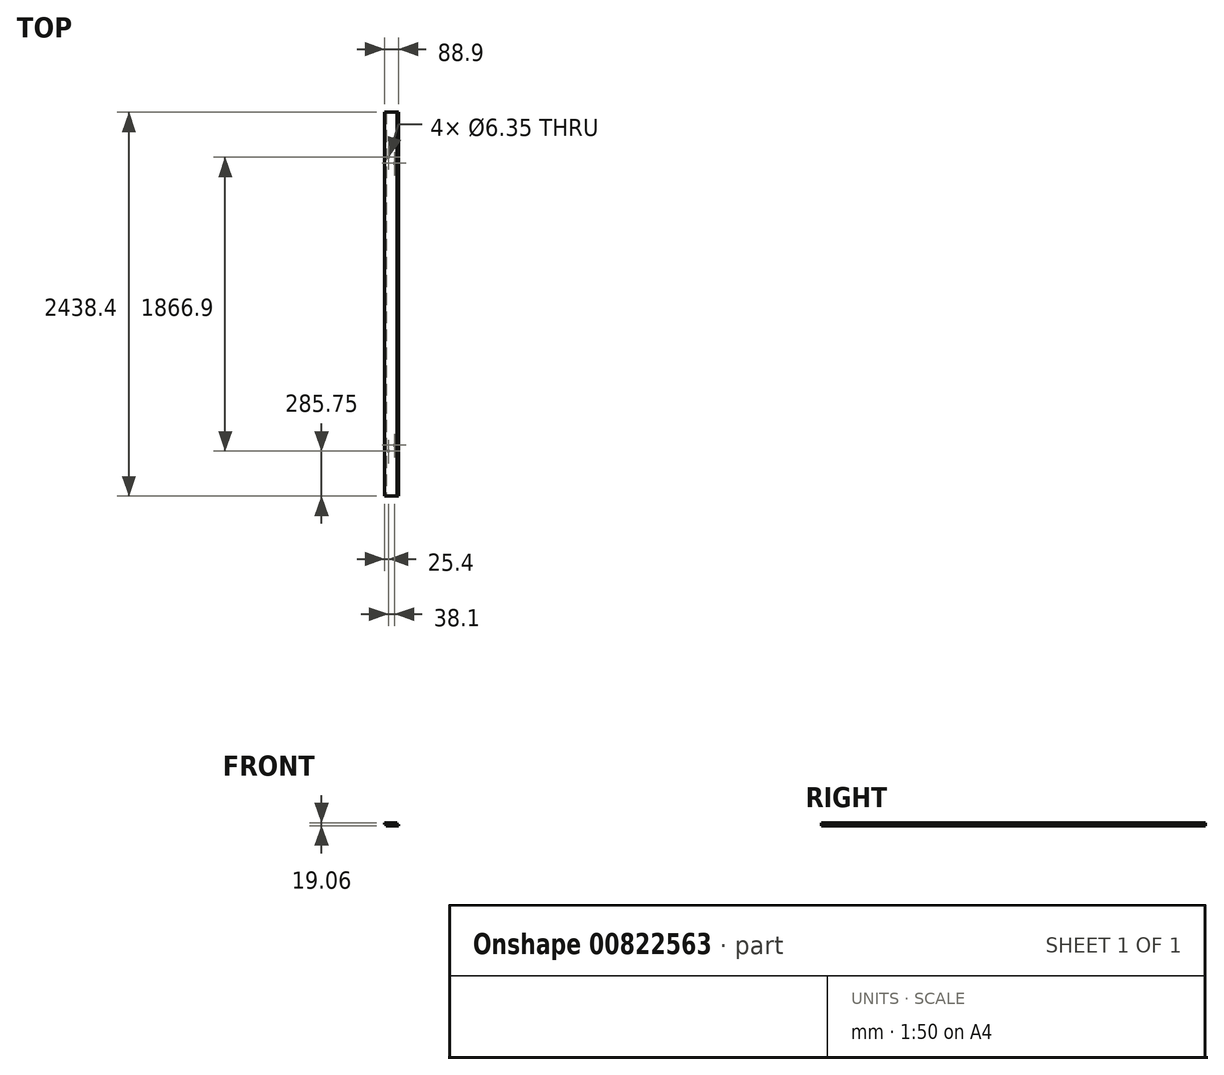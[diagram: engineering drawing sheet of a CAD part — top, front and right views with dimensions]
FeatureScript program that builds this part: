
annotation { "Feature Type Name" : "Feature", "Feature Type Description" : "" }
export const myFeature = defineFeature(function(context is Context, id is Id, definition is map)
    precondition{}
    {
        {
            var Q0;
            Q0=qCreatedBy(makeId("Front.planeOp"),FACE);
            var sketch = newSketch(context, id + "F0", { "sketchPlane" : qUnion([Q0])});
            skLineSegment(sketch, "E0.bottom", {"start": v(-44.45, 9.52) * mm, "end": v(44.45, 9.52) * mm});
            skLineSegment(sketch, "E0.top", {"start": v(-44.45, -9.52) * mm, "end": v(44.45, -9.52) * mm});
            skLineSegment(sketch, "E0.left", {"start": v(-44.45, 9.52) * mm, "end": v(-44.45, -9.53) * mm});
            skLineSegment(sketch, "E0.right", {"start": v(44.45, 9.52) * mm, "end": v(44.45, -9.53) * mm});
            skLineSegment(sketch, "E1", {"start": v(-44.45, -9.53) * mm, "end": v(44.45, 9.53) * mm, "construction": true});
            skSolve(sketch);
        }
        {
            var Q0;
            Q0=qSketchRegion(id+"F0",true);
            extrude(context, id + "F1", {"entities" : qUnion([Q0]), "endBound" : BoundingType.SYMMETRIC, "depth" : 2438.4 * mm, "offsetDistance" : 25.4 * mm});
        }
        {
            var Q0;
            Q0=makeQuery(id+"F1.opExtrude","CAP_FACE",FACE,{"disambiguationData":[OSD([sQuery(id+"F0.wireOp",EDGE,"E0.bottom"),sQuery(id+"F0.wireOp",EDGE,"E0.top"),sQuery(id+"F0.wireOp",EDGE,"E0.left"),sQuery(id+"F0.wireOp",EDGE,"E0.right")])],"isStart":false});
            var sketch = newSketch(context, id + "F2", { "sketchPlane" : qUnion([Q0])});
            skLineSegment(sketch, "E2.bottom", {"start": v(-82.02, 0) * mm, "end": v(-34.92, 0) * mm});
            skLineSegment(sketch, "E2.top", {"start": v(-82.02, -23.13) * mm, "end": v(-34.92, -23.13) * mm});
            skLineSegment(sketch, "E2.left", {"start": v(-82.02, 0) * mm, "end": v(-82.02, -23.13) * mm});
            skLineSegment(sketch, "E2.right", {"start": v(-34.92, 0) * mm, "end": v(-34.92, -23.13) * mm});
            skLineSegment(sketch, "E3.bottom", {"start": v(34.93, 22) * mm, "end": v(79.08, 22) * mm});
            skLineSegment(sketch, "E3.top", {"start": v(34.93, 0) * mm, "end": v(79.08, 0) * mm});
            skLineSegment(sketch, "E3.left", {"start": v(34.93, 22) * mm, "end": v(34.93, 0) * mm});
            skLineSegment(sketch, "E3.right", {"start": v(79.08, 22) * mm, "end": v(79.08, 0) * mm});
            skSolve(sketch);
        }
        {
            var Q0;
            Q0=qSketchRegion(id+"F2",true);
            extrude(context, id + "F3", {"entities" : qUnion([Q0]), "operationType" : NewBodyOperationType.REMOVE, "endBound" : BoundingType.THROUGH_ALL, "oppositeDirection" : true, "depth" : 25.4 * mm, "offsetDistance" : 25.4 * mm});
        }
        {
            var Q0;
            Q0=makeQuery(id+"F1.opExtrude","SWEPT_FACE",FACE,{"disambiguationData":[OSD([sQuery(id+"F0.wireOp",EDGE,"E0.bottom")])]});
            var sketch = newSketch(context, id + "F4", { "sketchPlane" : qUnion([Q0])});
            skLineSegment(sketch, "E4", {"start": v(0, 0) * mm, "end": v(0, -914.4) * mm, "construction": true});
            skLineSegment(sketch, "E5", {"start": v(-19.05, -914.4) * mm, "end": v(19.05, -914.4) * mm, "construction": true});
            skLineSegment(sketch, "E6.bottom", {"start": v(-19.05, -895.35) * mm, "end": v(19.05, -895.35) * mm, "construction": true});
            skLineSegment(sketch, "E6.top", {"start": v(-19.05, -933.45) * mm, "end": v(19.05, -933.45) * mm, "construction": true});
            skLineSegment(sketch, "E6.left", {"start": v(-19.05, -895.35) * mm, "end": v(-19.05, -933.45) * mm, "construction": true});
            skLineSegment(sketch, "E6.right", {"start": v(19.05, -895.35) * mm, "end": v(19.05, -933.45) * mm, "construction": true});
            skCircle(sketch, "E7", {"center": v(-19.05, -933.45) * mm, "radius": 3.18 * mm});
            skCircle(sketch, "E8", {"center": v(19.05, -895.35) * mm, "radius": 3.18 * mm});
            skLineSegment(sketch, "E9", {"start": v(0, 0) * mm, "end": v(61.5, 0) * mm, "construction": true});
            skPoint(sketch, "E9.endSnap0", {"position": v(34.93, 0) * mm});
            skCircle(sketch, "E10.MirrorC", {"center": v(-19.05, 933.45) * mm, "radius": 3.18 * mm});
            skCircle(sketch, "E11.MirrorC", {"center": v(19.05, 895.35) * mm, "radius": 3.18 * mm});
            skSolve(sketch);
        }
        {
            var Q0;
            Q0=qSketchRegion(id+"F4",true);
            extrude(context, id + "F5", {"entities" : qUnion([Q0]), "operationType" : NewBodyOperationType.REMOVE, "endBound" : BoundingType.THROUGH_ALL, "oppositeDirection" : true, "depth" : 25.4 * mm, "offsetDistance" : 25.4 * mm});
        }
    });
